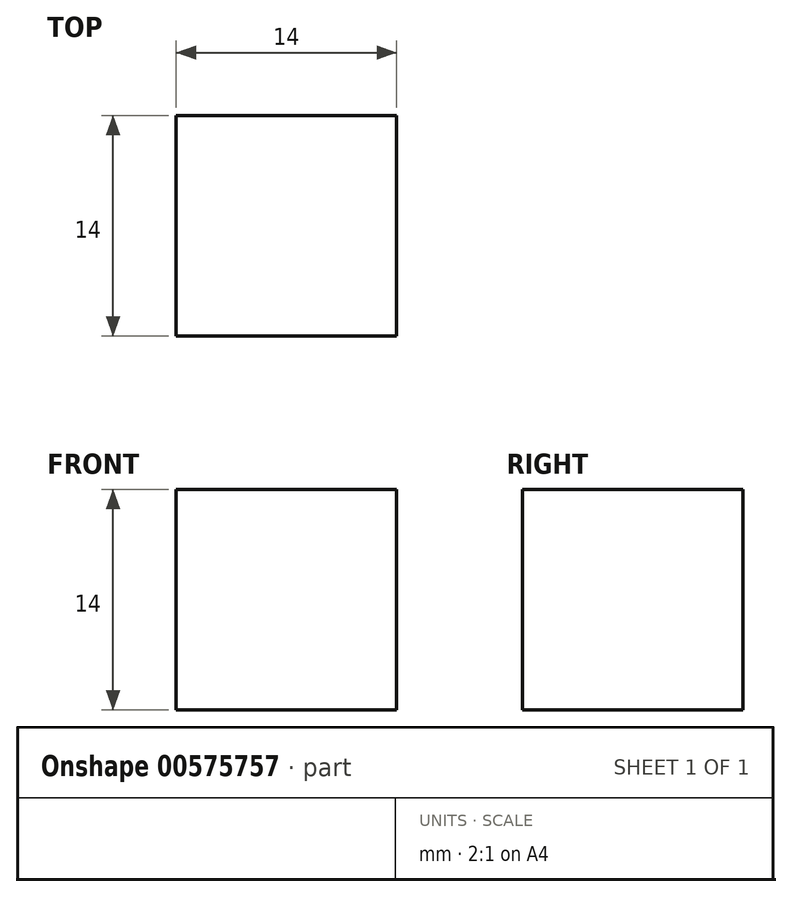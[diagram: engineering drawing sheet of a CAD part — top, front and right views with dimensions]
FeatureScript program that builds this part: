
annotation { "Feature Type Name" : "Feature", "Feature Type Description" : "" }
export const myFeature = defineFeature(function(context is Context, id is Id, definition is map)
    precondition{}
    {
        {
            var Q0;
            Q0=qCreatedBy(makeId("Top.planeOp"),FACE);
            var sketch = newSketch(context, id + "F0", { "sketchPlane" : qUnion([Q0])});
            skLineSegment(sketch, "E0.bottom", {"start": v(-7, 7) * mm, "end": v(7, 7) * mm});
            skLineSegment(sketch, "E0.top", {"start": v(-7, -7) * mm, "end": v(7, -7) * mm});
            skLineSegment(sketch, "E0.left", {"start": v(-7, 7) * mm, "end": v(-7, -7) * mm});
            skLineSegment(sketch, "E0.right", {"start": v(7, 7) * mm, "end": v(7, -7) * mm});
            skPoint(sketch, "E0.middle", {"position": v(0, 0) * mm});
            skSolve(sketch);
        }
        {
            var Q0;
            Q0 = qSketchRegion(id + "F0", true);
            extrude(context, id + "F1", {"entities" : qUnion([Q0]), "depth" : 14 * mm, "offsetDistance" : 25 * mm});
        }
    });
